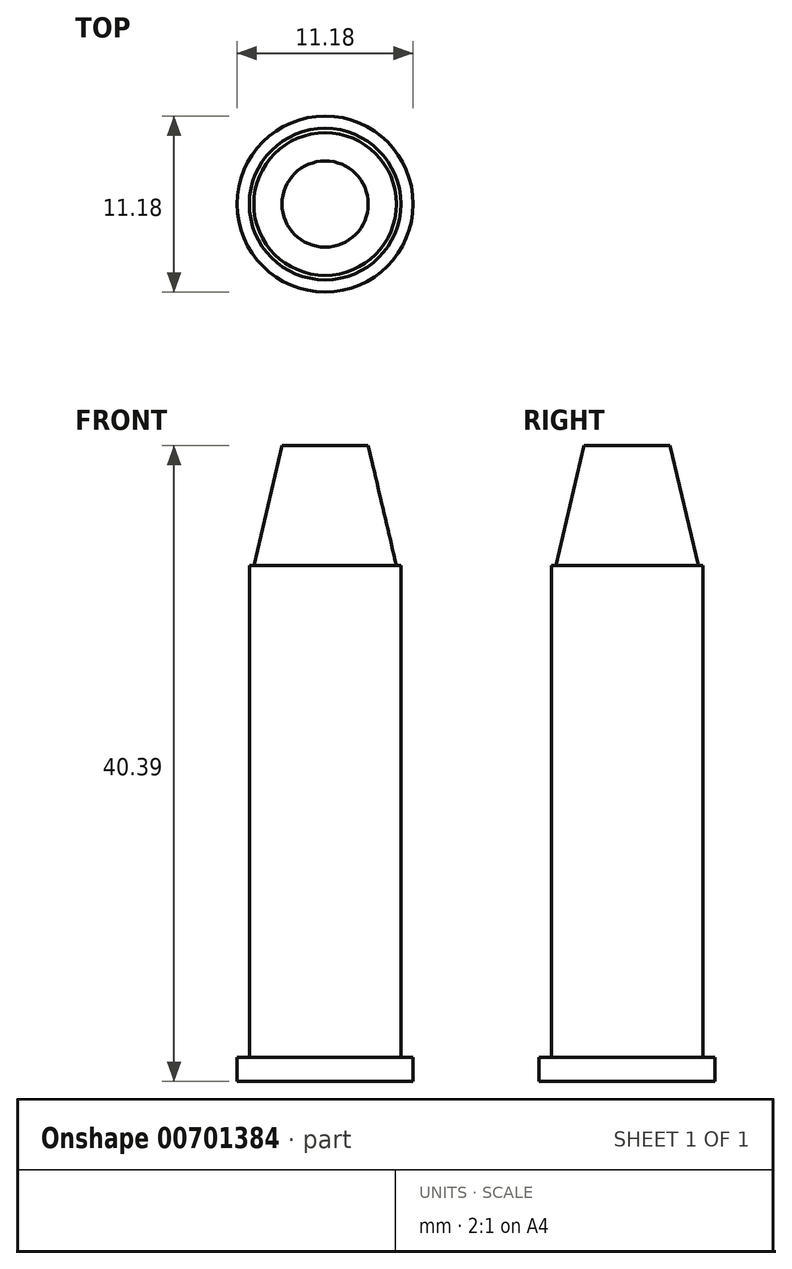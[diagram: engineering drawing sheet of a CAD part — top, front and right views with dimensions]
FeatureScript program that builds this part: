
annotation { "Feature Type Name" : "Feature", "Feature Type Description" : "" }
export const myFeature = defineFeature(function(context is Context, id is Id, definition is map)
    precondition{}
    {
        {
            var Q0;
            Q0=qCreatedBy(makeId("Front.planeOp"),FACE);
            var sketch = newSketch(context, id + "F0", { "sketchPlane" : qUnion([Q0])});
            skLineSegment(sketch, "E0", {"start": v(0, 0) * mm, "end": v(5.59, 0) * mm});
            skLineSegment(sketch, "E1", {"start": v(5.59, 0) * mm, "end": v(5.59, 1.52) * mm});
            skLineSegment(sketch, "E2", {"start": v(5.59, 1.52) * mm, "end": v(4.81, 1.52) * mm});
            skLineSegment(sketch, "E3", {"start": v(4.81, 1.52) * mm, "end": v(4.81, 32.77) * mm});
            skLineSegment(sketch, "E4", {"start": v(4.81, 32.77) * mm, "end": v(4.53, 32.77) * mm});
            skLineSegment(sketch, "E5", {"start": v(0, 40.39) * mm, "end": v(0, 0) * mm});
            skLineSegment(sketch, "E6", {"start": v(0, 40.39) * mm, "end": v(2.74, 40.39) * mm});
            skLineSegment(sketch, "E7", {"start": v(2.74, 40.39) * mm, "end": v(4.53, 32.77) * mm});
            skSolve(sketch);
        }
        {
            var Q0;
            Q0=makeQuery(id+"F0.imprint","IMPRINT",FACE,{"disambiguationData":[TD([[makeQuery(id+"F0.imprint","IMPRINT",EDGE,{"derivedFrom":sQuery(id+"F0.wireOp",EDGE,"E0")}),1.0]])]});
            var Q1;
            Q1=sQuery(id+"F0.wireOp",EDGE,"E5");
            revolve(context, id + "F1", {"entities" : qUnion([Q0]), "axis" : qUnion([Q1]), "revolveType" : RevolveType.FULL});
        }
    });
